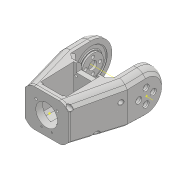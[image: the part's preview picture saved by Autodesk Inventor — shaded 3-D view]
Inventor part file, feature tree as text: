
AUTODESK INVENTOR PART (.ipt)
format: ipt  version: 2018 (Build 220112000, 112)  size: 1,153,024 bytes
history: native  units: mm
features: projected_geometry x49, sketch x46, extrude x38, hole x13, fillet x12, other x10, chamfer x6, reference x3, mirror x1, plane x1
ambient origin geometry x8: Origin, YZ Plane, XZ Plane, XY Plane, X Axis, Y Axis, Z Axis, Center Point
bodies: Solid1 (feature_tree)
feature tree (179):
  extrude  "Extrusion1"  Depth=45.0mm
  extrude  "Extrusion2"  Depth=2.25mm
  hole  "Hole1"  [1 undecoded]
  hole  "Hole2"  [1 undecoded]
  fillet  "Fillet1"  Radius=14.0mm
  extrude  "Extrusion3"  Depth=18.5mm
  extrude  "Extrusion4"  Depth=10.0mm
  extrude  "Extrusion5"  Depth=2.0mm
  extrude  "Extrusion6"  Depth=2.0mm
  hole  "Hole3"  [1 undecoded]
  extrude  "Extrusion7"  Depth=2.0mm
  extrude  "Extrusion8"  Depth=1.0mm TaperAngle=0.0deg
  extrude  "Extrusion9"  Depth=24.5mm
  extrude  "Extrusion10"  Depth=10.0mm
  extrude  "Extrusion11"  Depth=14.5mm
  extrude  "Extrusion13"  Depth=14.5mm
  extrude  "Extrusion14"  Depth=5.0mm
  extrude  "Extrusion15"  Depth=2.25mm
  extrude  "Extrusion16"  Depth=5.0mm
  extrude  "Extrusion17"  Depth=9.0mm
  chamfer  "Chamfer1"  Distance=1.0mm
  fillet  "Fillet7"  Radius=20.7mm
  fillet  "Fillet8"  Radius=32.0mm
  mirror  "Mirror1"
  sketch  "Sketch26"  dims[d55=2.25mm d56=5.0mm]
  extrude  "Extrusion24"  Depth=1.0mm TaperAngle=0.0deg
  extrude  "Extrusion25"  Depth=8.0mm
  extrude  "Extrusion26"  Depth=0.2mm TaperAngle=0.0deg
  extrude  "Extrusion27"  Depth=5.0mm TaperAngle=0.0deg
  other  "Work Axis1"
  plane  "Work Plane2"
  extrude  "Extrusion28"  Depth=0.2mm TaperAngle=0.0deg
  extrude  "Extrusion29"  Depth=2.0mm TaperAngle=45.0deg
  extrude  "Extrusion31"  Depth=0.5mm
  extrude  "Extrusion32"  Depth=36.0mm
  extrude  "Extrusion33"  Depth=60.0mm
  sketch  "Sketch41"  dims[d100=0.2mm d101=0.0mm d102=2.5mm d103=2.0mm d104=45.0deg]
  extrude  "Extrusion34"  Depth=2.3mm
  chamfer  "Chamfer6"  Distance=15.0mm
  fillet  "Fillet9"  Radius=15.0mm
  extrude  "Extrusion35"  Depth=15.0mm TaperAngle=0.0deg
  extrude  "Extrusion36"  Depth=41.5mm
  fillet  "Fillet10"  Radius=15.5mm
  extrude  "Extrusion37"  Depth=5.0mm
  extrude  "Extrusion38"  Depth=100.0mm TaperAngle=0.0deg
  extrude  "Extrusion39"  Depth=11.5mm
  extrude  "Extrusion40"  Depth=11.5mm
  hole  "Hole6"  [1 undecoded]
  fillet  "Fillet12"  Radius=100.0mm
  extrude  "Extrusion41"  Depth=100.0mm TaperAngle=0.0deg
  extrude  "Extrusion42"  Depth=2.0mm
  hole  "Hole7"  [1 undecoded]
  extrude  "Extrusion43"  Depth=1.0mm TaperAngle=0.0deg
  extrude  "Extrusion44"  Depth=2.0mm
  sketch  "Sketch58"  dims[d202=15.0deg d204=10.970628mm]
  hole  "Hole8"  [1 undecoded]
  hole  "Hole9"  [1 undecoded]
  hole  "Hole10"  [1 undecoded]
  hole  "Hole11"  [1 undecoded]
  hole  "Hole12"  [1 undecoded]
  hole  "Hole13"  [1 undecoded]
  hole  "Hole14"  [1 undecoded]
  hole  "Hole15"  [1 undecoded]
  chamfer  "Chamfer10"  Distance=0.75mm
  chamfer  "Chamfer11"  Distance=20.5mm
  chamfer  "Chamfer12"  Distance=3.05mm
  chamfer  "Chamfer13"  Distance=14.0mm
  extrude  "Extrusion45"  Depth=0.6mm
  fillet  "Fillet13"  Radius=1.55mm
  extrude  "Extrusion46"  Depth=0.6mm
  fillet  "Fillet14"  Radius=2.5mm
  fillet  "Fillet15"  Radius=8.0mm
  fillet  "Fillet16"  Radius=2.5mm
  fillet  "Fillet17"  Radius=4.624622mm
  fillet  "Fillet18"  Radius=4.624622mm
  sketch  "Sketch1"  dims[d0=24.5mm d1=45.0mm]
  sketch  "Sketch2"  dims[d2=1.95mm d3=0.0mm d4=2.25mm]
  projected_geometry  "Projected Loop1"
  sketch  "Sketch3"  dims[d5=20.0mm d6=2.25mm]
  projected_geometry  "Projected Loop2"
  sketch  "Sketch4"  dims[d7=5.25mm d8=5.25mm d9=14.0mm]
  projected_geometry  "Projected Loop3"
  sketch  "Sketch5"  dims[d10=5.25mm d11=18.5mm]
  projected_geometry  "Projected Loop4"
  sketch  "Sketch6"  dims[d12=10.0mm d13=0.0mm d14=20.5mm]
  projected_geometry  "Projected Loop5"
  sketch  "Sketch7"  dims[d15=2.0mm d16=2.195mm]
  projected_geometry  "Projected Loop6"
  sketch  "Sketch8"  dims[d17=2.0mm]
  projected_geometry  "Projected Loop7"
  sketch  "Sketch9"  dims[d18=2.4mm d19=6.0mm d20=4.4mm d21=2.0mm d22=90.0deg d23=8.0mm d24=20.594885mm d25=20.5mm]
  projected_geometry  "Projected Loop8"
  projected_geometry  "Projected Loop9"
  sketch  "Sketch10"  dims[d26=26.65mm d27=2.0mm]
  projected_geometry  "Projected Loop10"
  projected_geometry  "Projected Loop11"
  sketch  "Sketch11"  dims[d28=2.0mm]
  projected_geometry  "Projected Loop12"
  sketch  "Sketch12"  dims[d29=2.4mm d30=6.0mm d31=4.4mm d32=2.0mm d33=90.0deg d34=8.0mm d35=20.594885mm d36=0.5mm]
  sketch  "Sketch13"  dims[d37=18.0mm d38=1.0mm d39=0.0mm]
  sketch  "Sketch14"  dims[d41=5.0mm d42=0.0mm d43=24.5mm]
  projected_geometry  "Projected Loop13"
  sketch  "Sketch16"  dims[d44=1.15mm d45=0.0mm d46=10.0mm]
  projected_geometry  "Projected Loop14"
  sketch  "Sketch17"  dims[d47=21.0mm d48=14.5mm]
  projected_geometry  "Projected Loop15"
  sketch  "Sketch18"  dims[d49=20.0mm d50=14.5mm]
  projected_geometry  "Projected Loop16"
  sketch  "Sketch19"  dims[d51=24.5mm d52=5.0mm]
  projected_geometry  "Projected Loop17"
  sketch  "Sketch20"  dims[d53=5.0mm d54=2.25mm]
  projected_geometry  "Projected Loop18"
  projected_geometry  "Projected Loop25"
  sketch  "Sketch31"  dims[d57=5.0mm d58=9.0mm]
  projected_geometry  "Projected Loop30"
  reference  "Reference1"
  sketch  "Sketch32"  dims[d59=14.75mm]
  projected_geometry  "Projected Loop31"
  sketch  "Sketch33"  dims[d60=4.0mm d61=1.0mm d62=0.0mm d63=20.7mm]
  projected_geometry  "Projected Loop32"
  sketch  "Sketch34"  dims[d64=2.3mm d65=6.0mm d66=4.4mm d67=2.0mm d68=90.0deg d69=8.0mm d70=20.594885mm d72=32.0mm]
  projected_geometry  "Projected Loop33"
  other  "Work Point1"
  other  "Work Point2"
  other  "Work Point3"
  sketch  "Sketch35"  dims[d73=3.0mm d74=0.0mm d75=1.0mm d76=0.0mm]
  sketch  "Sketch37"  dims[d77=12.25mm d78=0.0mm d80=8.0mm]
  projected_geometry  "Projected Loop34"
  sketch  "Sketch38"  dims[d81=4.5mm d82=0.0mm d84=0.2mm d85=0.0mm]
  sketch  "Sketch39"  dims[d91=8.0mm d92=0.0mm d93=5.0mm d94=0.0mm]
  sketch  "Sketch40"  dims[d95=5.0mm d96=0.0mm d98=0.2mm d99=0.0mm]
  projected_geometry  "Projected Loop35"
  projected_geometry  "Projected Loop36"
  projected_geometry  "Projected Loop37"
  projected_geometry  "Projected Loop38"
  sketch  "Sketch42"  dims[d105=1.5mm d114=0.5mm]
  projected_geometry  "Projected Loop39"
  sketch  "Sketch43"  dims[d130=60.0mm d131=36.0mm]
  reference  "Reference2"
  reference  "Reference3"
  sketch  "Sketch45"  dims[d146=40.0mm d147=60.0mm]
  projected_geometry  "Projected Loop40"
  sketch  "Sketch46"  dims[d148=0.0mm d149=2.3mm d150=15.0mm d151=0.0mm d152=15.0mm d153=0.0mm]
  projected_geometry  "Projected Loop41"
  sketch  "Sketch48"  dims[d154=15.0mm d155=0.0mm d156=15.0mm d157=0.0mm]
  projected_geometry  "Projected Loop43"
  sketch  "Sketch49"  dims[d158=20.5mm d159=41.5mm d160=15.5mm]
  projected_geometry  "Projected Loop44"
  projected_geometry  "Projected Loop45"
  sketch  "Sketch50"  dims[d161=15.5mm d162=5.0mm]
  projected_geometry  "Projected Loop46"
  sketch  "Sketch52"  dims[d165=100.0mm d166=0.0mm d167=100.0mm d168=0.0mm]
  sketch  "Sketch53"  dims[d172=0.0mm d173=11.5mm]
  projected_geometry  "Projected Loop47"
  sketch  "Sketch54"  dims[d175=11.5mm d176=11.5mm]
  projected_geometry  "Projected Loop48"
  sketch  "Sketch55"  dims[d179=100.0mm d180=0.0mm d187=7.0mm d188=100.0mm d189=0.0mm]
  sketch  "Sketch56"  dims[d193=100.0mm d194=0.0mm d195=100.0mm d196=0.0mm]
  projected_geometry  "Projected Loop49"
  sketch  "Sketch57"  dims[d197=5.0mm d198=2.0mm d199=45.0deg d200=8.0mm]
  projected_geometry  "Projected Loop50"
  projected_geometry  "Projected Loop51"
  projected_geometry  "Projected Loop52"
  projected_geometry  "Projected Loop53"
  projected_geometry  "Projected Loop55"
  projected_geometry  "Projected Loop56"
  projected_geometry  "Projected Loop57"
  sketch  "Sketch59"  dims[d205=15.470628mm d206=1.0mm d207=0.0mm]
  projected_geometry  "Projected Loop58"
  sketch  "Sketch60"  dims[d208=1.0mm d209=0.0mm d213=2.0mm d215=15.0deg d216=4.0mm d217=4.0mm d218=5.0mm d219=0.0mm d222=32.0mm d223=4.0mm d224=0.0mm d225=2.5mm d226=0.0mm d227=6.5mm d228=0.0mm d235=1.567mm d236=15.0mm d237=4.0mm d238=2.0mm d239=90.0deg d240=15.0mm d241=20.594885mm d243=0.75mm d244=20.5mm d245=3.05mm d246=0.0mm d247=14.0mm d248=3.2mm d249=6.0mm d250=4.0mm d251=2.0mm d252=90.0deg d253=8.8mm d254=20.594885mm d255=20.5mm d256=1.55mm d257=0.0mm d258=8.0mm d259=2.5mm d260=0.0mm d261=8.0mm d262=2.5mm d263=0.0mm d266=4.624622mm d267=4.624622mm d268=2.75mm d269=2.75mm d270=2.35mm d271=2.35mm d272=14.0mm d273=4.0mm d274=5.6mm d275=3.708mm d276=3.023mm d277=2.0mm d278=14.3117mm d279=17.0mm d280=0.0mm d281=4.0mm d282=3.708mm d283=3.023mm d284=2.0mm d285=14.3117mm d286=19.0mm d287=0.0mm d288=4.0mm d289=3.708mm d290=3.023mm d291=2.0mm d292=14.3117mm d293=20.0mm d294=0.0mm d295=2.3mm d296=4.0mm d297=4.4mm d298=2.0mm d299=90.0deg d300=32.25mm d301=0.0mm d302=3.3mm d303=4.0mm d304=6.3mm d305=2.0mm d306=90.0deg d307=32.25mm d308=0.0mm d309=1.567mm d310=4.0mm d311=6.3mm d312=2.0mm d313=90.0deg d314=45.0mm d315=20.594885mm d316=1.567mm d317=4.0mm d318=6.3mm d319=2.0mm d320=90.0deg d321=55.0mm d322=20.594885mm d323=2.459mm d324=6.0mm d325=6.3mm d326=2.0mm d327=90.0deg d328=50.0mm d329=20.594885mm d330=3.0mm d331=2.0mm d332=45.0deg d333=5.0mm d334=20.0mm d335=45.0deg d336=5.0mm d337=20.0mm d338=45.0deg d339=5.0mm d340=20.0mm d341=45.0deg d342=6.0mm d343=6.0mm d344=6.0mm d345=6.0mm d346=2.0mm d347=0.0mm d348=1.5mm d349=6.0mm d350=6.0mm d351=6.0mm d352=6.0mm d353=3.0mm d354=0.0mm d355=1.5mm d356=0.4mm d357=0.4mm d358=0.3mm d359=1.0mm d360=0.6mm]
  projected_geometry  "Projected Loop59"
  parser-record x1  (decoder bookkeeping rows leaked as tree rows — omitted from the tree; the rows remain in map.json)
  other  "servocheck.iam"
  other  "LX-16A:3"
  other  "DUOPAN-SG-SJ_10"
  projected_geometry  "Project Cut Edges1"
  projected_geometry  "Project Cut Edges3"
  other  "bottomarm:1"
  other  "arm1:1"
note: 13 required parameter values undecoded (feature->parameter linkage not recoverable at this tier; creation-order binding heuristic only, values carry confidence <= 0.55)
note: 1 file-system path scrubbed to <path> (originals preserved in map.json)
